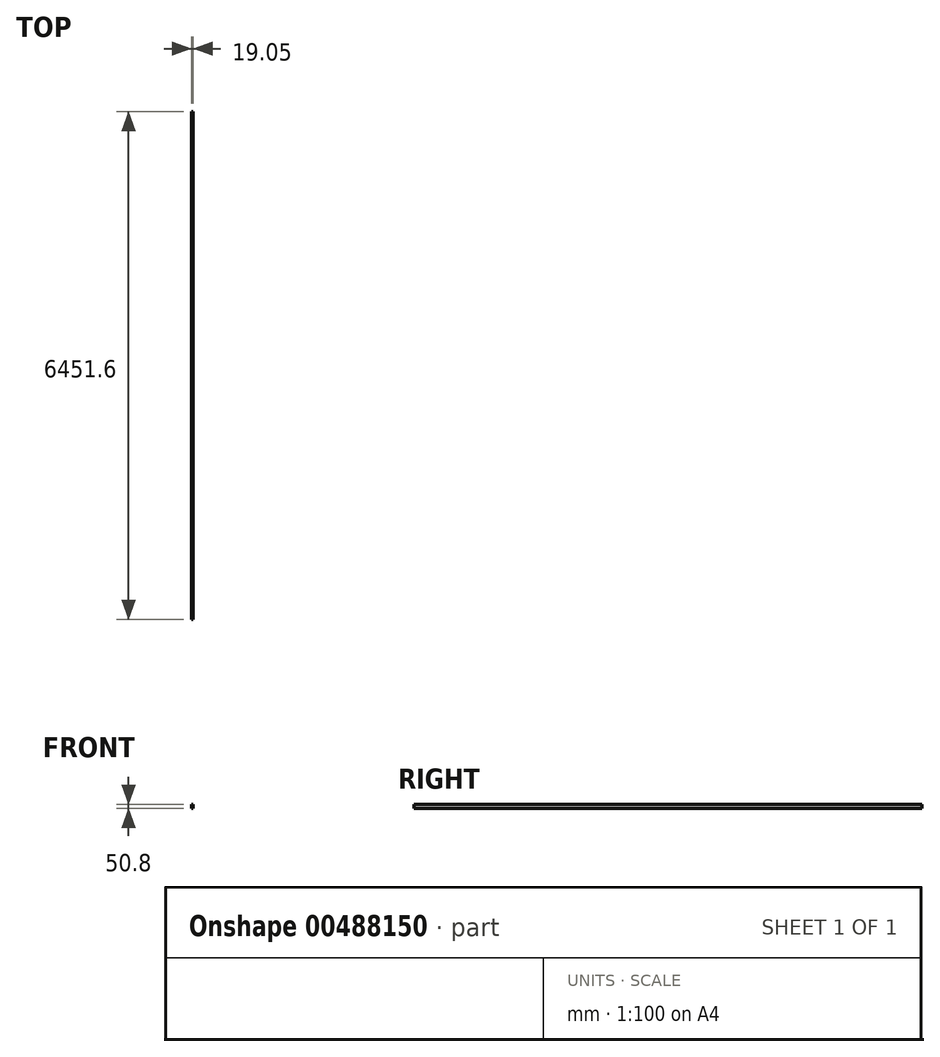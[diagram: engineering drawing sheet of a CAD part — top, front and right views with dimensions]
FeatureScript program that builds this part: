
annotation { "Feature Type Name" : "Feature", "Feature Type Description" : "" }
export const myFeature = defineFeature(function(context is Context, id is Id, definition is map)
    precondition{}
    {
        {
            var Q0;
            Q0=qCreatedBy(makeId("Front.planeOp"),FACE);
            var sketch = newSketch(context, id + "F0", { "sketchPlane" : qUnion([Q0])});
            skLineSegment(sketch, "E0", {"start": v(0, 0) * mm, "end": v(19.05, 0) * mm});
            skLineSegment(sketch, "E1", {"start": v(0, 0) * mm, "end": v(0, -50.8) * mm});
            skLineSegment(sketch, "E2", {"start": v(0, -50.8) * mm, "end": v(19.05, -50.8) * mm});
            skLineSegment(sketch, "E3", {"start": v(19.05, -50.8) * mm, "end": v(19.05, 0) * mm});
            skSolve(sketch);
        }
        {
            var Q0;
            Q0=makeQuery(id+"F0.imprint","IMPRINT",FACE,{"disambiguationData":[TD([[makeQuery(id+"F0.imprint","IMPRINT",EDGE,{"derivedFrom":sQuery(id+"F0.wireOp",EDGE,"E0")}),-1.0]])]});
            extrude(context, id + "F1", {"entities" : qUnion([Q0]), "oppositeDirection" : true, "depth" : 6451.6 * mm, "offsetDistance" : 25.4 * mm});
        }
    });
